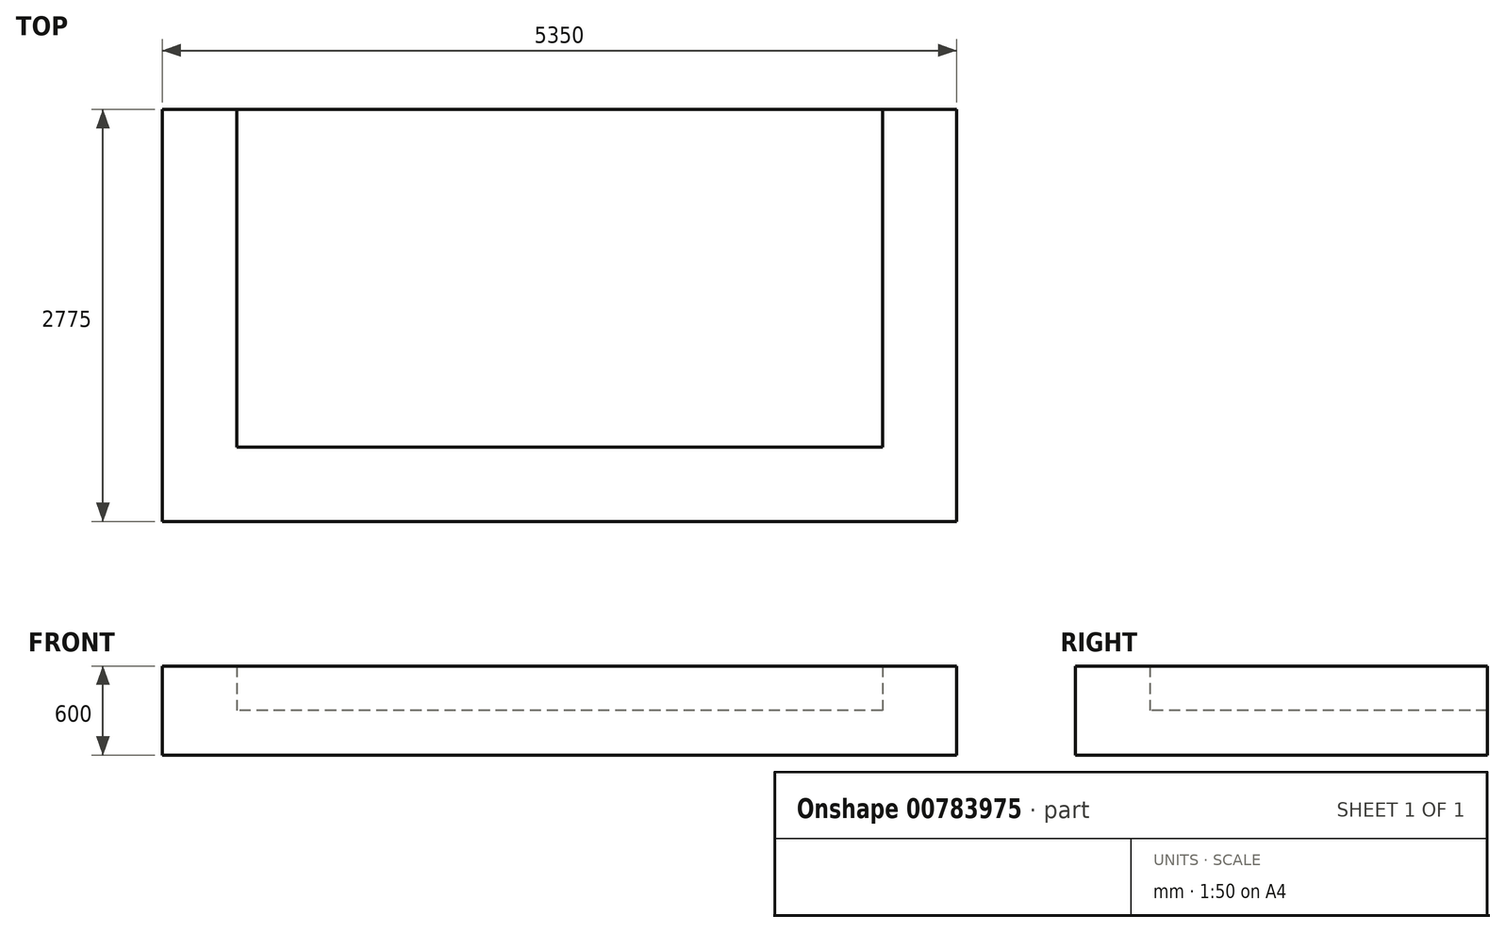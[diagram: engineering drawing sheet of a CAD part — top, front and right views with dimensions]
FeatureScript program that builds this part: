
annotation { "Feature Type Name" : "Feature", "Feature Type Description" : "" }
export const myFeature = defineFeature(function(context is Context, id is Id, definition is map)
    precondition{}
    {
        {
            var Q0;
            Q0=qCreatedBy(makeId("Top.planeOp"),FACE);
            var sketch = newSketch(context, id + "F0", { "sketchPlane" : qUnion([Q0])});
            skLineSegment(sketch, "E0.top", {"start": v(2175, -1137.5) * mm, "end": v(-2175, -1137.5) * mm});
            skLineSegment(sketch, "E0.left", {"start": v(2175, 1137.5) * mm, "end": v(2175, -1137.5) * mm});
            skLineSegment(sketch, "E0.right", {"start": v(-2175, 1137.5) * mm, "end": v(-2175, -1137.5) * mm});
            skPoint(sketch, "E0.middle", {"position": v(0, 0) * mm});
            skLineSegment(sketch, "E1", {"start": v(-2175, 1137.5) * mm, "end": v(-2675, 1137.5) * mm});
            skLineSegment(sketch, "E2", {"start": v(-2675, 1137.5) * mm, "end": v(-2675, -1637.5) * mm});
            skLineSegment(sketch, "E3", {"start": v(-2675, -1637.5) * mm, "end": v(2675, -1637.5) * mm});
            skLineSegment(sketch, "E4", {"start": v(2675, -1637.5) * mm, "end": v(2675, 1137.5) * mm});
            skLineSegment(sketch, "E5", {"start": v(2675, 1137.5) * mm, "end": v(2175, 1137.5) * mm});
            skSolve(sketch);
        }
        {
            var Q0;
            Q0=makeQuery(id+"F0.imprint","IMPRINT",FACE,{"disambiguationData":[TD([[makeQuery(id+"F0.imprint","IMPRINT",EDGE,{"derivedFrom":sQuery(id+"F0.wireOp",EDGE,"E0.top")}),1.0]])]});
            extrude(context, id + "F1", {"entities" : qUnion([Q0]), "depth" : 300 * mm, "offsetDistance" : 25 * mm});
        }
        {
            var Q0;
            Q0=makeQuery(id+"F1.opExtrude","CAP_FACE",FACE,{"disambiguationData":[OSD([sQuery(id+"F0.wireOp",EDGE,"E0.top"),sQuery(id+"F0.wireOp",EDGE,"E0.left"),sQuery(id+"F0.wireOp",EDGE,"E0.right"),sQuery(id+"F0.wireOp",EDGE,"E1"),sQuery(id+"F0.wireOp",EDGE,"E2"),sQuery(id+"F0.wireOp",EDGE,"E3"),sQuery(id+"F0.wireOp",EDGE,"E4"),sQuery(id+"F0.wireOp",EDGE,"E5")])],"isStart":true});
            var sketch = newSketch(context, id + "F2", { "sketchPlane" : qUnion([Q0])});
            skLineSegment(sketch, "E6.bottom", {"start": v(-2675, 1637.5) * mm, "end": v(2675, 1637.5) * mm});
            skLineSegment(sketch, "E6.top", {"start": v(-2675, -1137.5) * mm, "end": v(2675, -1137.5) * mm});
            skLineSegment(sketch, "E6.left", {"start": v(-2675, 1637.5) * mm, "end": v(-2675, -1137.5) * mm});
            skLineSegment(sketch, "E6.right", {"start": v(2675, 1637.5) * mm, "end": v(2675, -1137.5) * mm});
            skSolve(sketch);
        }
        {
            var Q0;
            Q0=makeQuery(id+"F2.imprint","IMPRINT",FACE,{"disambiguationData":[TD([[makeQuery(id+"F2.imprint","IMPRINT",EDGE,{"derivedFrom":sQuery(id+"F2.wireOp",EDGE,"E6.bottom")}),-1.0]])]});
            var Q1;
            Q1=makeQuery(id+"F2.imprint","IMPRINT",FACE,{"disambiguationData":[TD([[makeQuery(id+"F2.imprint","IMPRINT",EDGE,{"derivedFrom":makeQuery(id+"F1.opExtrude","CAP_EDGE",EDGE,{"disambiguationData":[OSD([sQuery(id+"F0.wireOp",EDGE,"E0.top")])],"isStart":true})}),1.0]])]});
            extrude(context, id + "F3", {"entities" : qUnion([Q0, Q1]), "operationType" : NewBodyOperationType.ADD, "depth" : 300 * mm, "offsetDistance" : 25 * mm});
        }
    });
